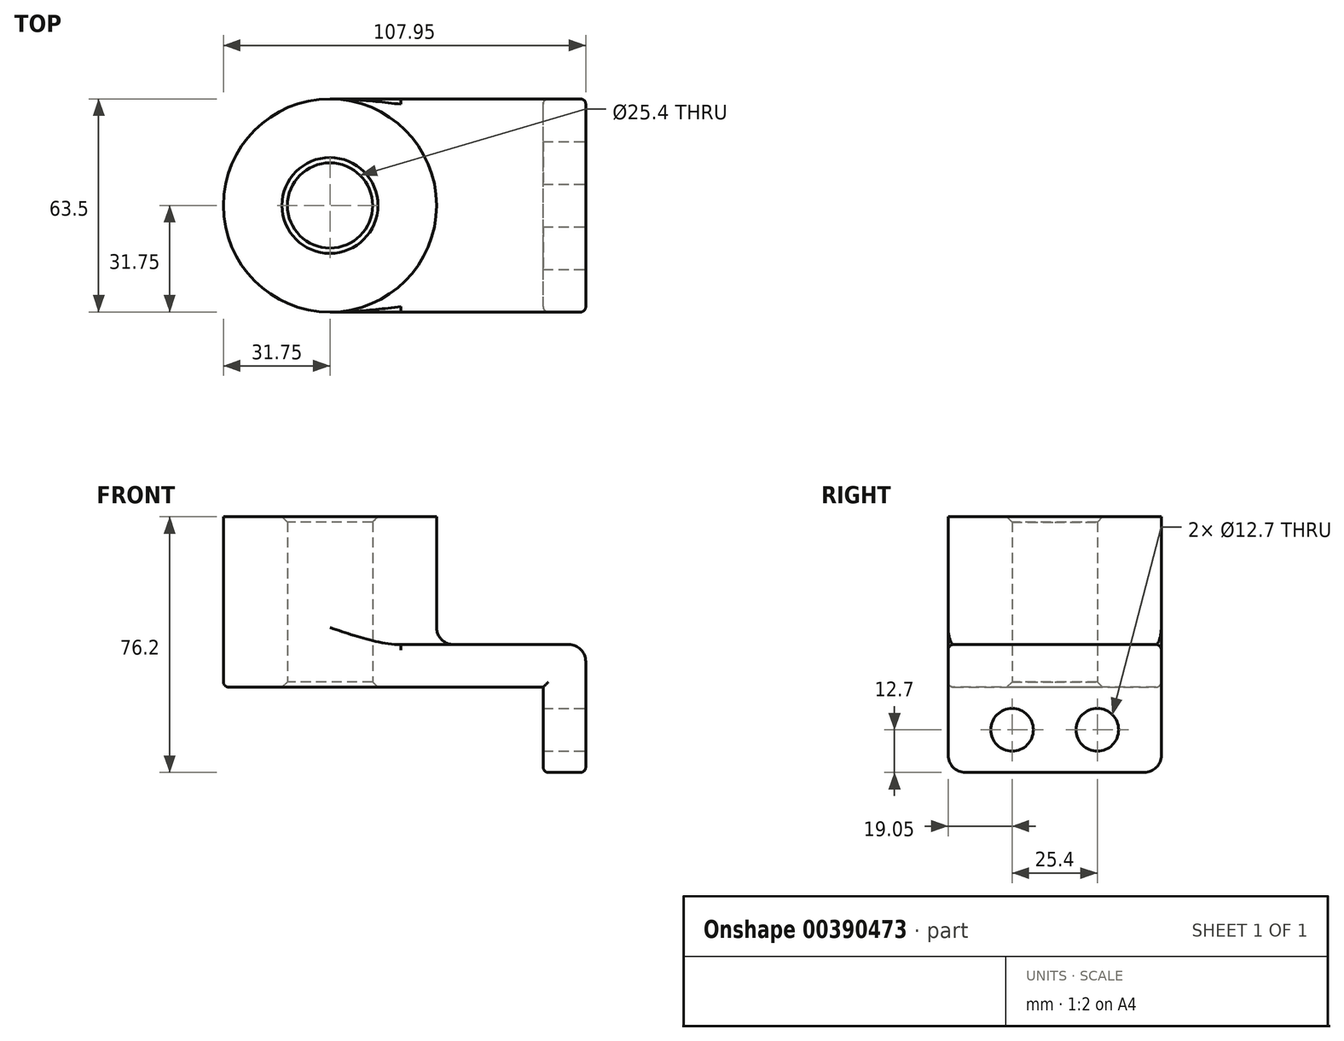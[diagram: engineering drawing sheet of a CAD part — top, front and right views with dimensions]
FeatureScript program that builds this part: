
annotation { "Feature Type Name" : "Feature", "Feature Type Description" : "" }
export const myFeature = defineFeature(function(context is Context, id is Id, definition is map)
    precondition{}
    {
        {
            var Q0;
            Q0=qCreatedBy(makeId("Top.planeOp"),FACE);
            var sketch = newSketch(context, id + "F0", { "sketchPlane" : qUnion([Q0])});
            skLineSegment(sketch, "E0.bottom", {"start": v(38.1, -31.75) * mm, "end": v(-38.1, -31.75) * mm});
            skLineSegment(sketch, "E0.top", {"start": v(38.1, 31.75) * mm, "end": v(-38.1, 31.75) * mm});
            skLineSegment(sketch, "E0.left", {"start": v(38.1, -31.75) * mm, "end": v(38.1, 31.75) * mm});
            skLineSegment(sketch, "E0.right", {"start": v(-38.1, -31.75) * mm, "end": v(-38.1, 31.75) * mm});
            skPoint(sketch, "E0.middle", {"position": v(0, 0) * mm});
            skCircle(sketch, "E1", {"center": v(-38.1, 0) * mm, "radius": 31.75 * mm});
            skCircle(sketch, "E2", {"center": v(-38.1, 0) * mm, "radius": 12.7 * mm});
            skSolve(sketch);
        }
        {
            var Q0;
            Q0 = qSketchRegion(id + "F0", true);
            extrude(context, id + "F1", {"entities" : qUnion([Q0]), "depth" : 12.7 * mm});
        }
        {
            var Q0;
            {var subQ1=sQuery(id+"F0.wireOp",EDGE,"E0.right");var subQ3=sQuery(id+"F0.wireOp",EDGE,"E2");var subQ4=makeQuery(id+"F0.imprint","INTERSECT",VERTEX,{"disambiguationData":[OD(0.0)],"derivedFrom":[subQ1,subQ3]});Q0=makeQuery(id+"F0.imprint","IMPRINT",FACE,{"disambiguationData":[TD([[makeQuery(id+"F0.imprint","IMPRINT",EDGE,{"disambiguationData":[TD([[subQ4,1.0]])],"derivedFrom":subQ3}),-1.0]])]});}
            var Q1;
            {var subQ1=sQuery(id+"F0.wireOp",EDGE,"E0.right");var subQ3=sQuery(id+"F0.wireOp",EDGE,"E2");var subQ4=makeQuery(id+"F0.imprint","INTERSECT",VERTEX,{"disambiguationData":[OD(0.0)],"derivedFrom":[subQ1,subQ3]});Q1=makeQuery(id+"F0.imprint","IMPRINT",FACE,{"disambiguationData":[TD([[makeQuery(id+"F0.imprint","IMPRINT",EDGE,{"disambiguationData":[TD([[subQ4,-1.0]])],"derivedFrom":subQ3}),-1.0]])]});}
            extrude(context, id + "F2", {"entities" : qUnion([Q0, Q1]), "operationType" : NewBodyOperationType.ADD, "depth" : 50.8 * mm});
        }
        {
            var Q0;
            Q0=makeQuery(id+"F1.opExtrude","SWEPT_FACE",FACE,{"disambiguationData":[OSD([sQuery(id+"F0.wireOp",EDGE,"E0.left")])]});
            var sketch = newSketch(context, id + "F3", { "sketchPlane" : qUnion([Q0])});
            skLineSegment(sketch, "E3.bottom", {"start": v(-31.75, 12.7) * mm, "end": v(31.75, 12.7) * mm});
            skLineSegment(sketch, "E3.top", {"start": v(-31.75, -25.4) * mm, "end": v(31.75, -25.4) * mm});
            skLineSegment(sketch, "E3.left", {"start": v(-31.75, 12.7) * mm, "end": v(-31.75, -25.4) * mm});
            skLineSegment(sketch, "E3.right", {"start": v(31.75, 12.7) * mm, "end": v(31.75, -25.4) * mm});
            skCircle(sketch, "E4", {"center": v(-12.7, -12.7) * mm, "radius": 6.35 * mm});
            skLineSegment(sketch, "E5", {"start": v(0, 12.7) * mm, "end": v(0, -25.4) * mm, "construction": true});
            skCircle(sketch, "E6.MirrorC", {"center": v(12.7, -12.7) * mm, "radius": 6.35 * mm});
            skSolve(sketch);
        }
        {
            var Q0;
            {var subQ2=sQuery(id+"F3.wireOp",EDGE,"E3.top");Q0=makeQuery(id+"F3.imprint","IMPRINT",FACE,{"disambiguationData":[TD([[makeQuery(id+"F3.imprint","IMPRINT",EDGE,{"derivedFrom":subQ2}),1.0]])]});}
            var Q1;
            {var subQ0=sQuery(id+"F3.wireOp",EDGE,"E3.bottom");Q1=makeQuery(id+"F3.imprint","IMPRINT",FACE,{"disambiguationData":[TD([[makeQuery(id+"F3.imprint","IMPRINT",EDGE,{"derivedFrom":subQ0}),-1.0]])]});}
            extrude(context, id + "F4", {"entities" : qUnion([Q0, Q1]), "operationType" : NewBodyOperationType.ADD, "oppositeDirection" : true, "depth" : 12.7 * mm});
        }
        {
            var Q0;
            {var subQ0=sQuery(id+"F0.wireOp",EDGE,"E1");Q0=makeQuery(id+"F2.boolean.opBoolean","INTERSECT",EDGE,{"derivedFrom":[makeQuery(id+"F1.opExtrude","CAP_FACE",FACE,{"disambiguationData":[OSD([sQuery(id+"F0.wireOp",EDGE,"E0.bottom"),sQuery(id+"F0.wireOp",EDGE,"E0.top"),sQuery(id+"F0.wireOp",EDGE,"E0.left"),subQ0,sQuery(id+"F0.wireOp",EDGE,"E2")])],"isStart":false}),makeQuery(id+"F2.opExtrude","SWEPT_FACE",FACE,{"disambiguationData":[OSD([subQ0])]})]});}
            var Q1;
            Q1=makeQuery(id+"F1.opExtrude","CAP_EDGE",EDGE,{"disambiguationData":[OSD([sQuery(id+"F0.wireOp",EDGE,"E0.left")])],"isStart":false});
            var Q2;
            Q2=makeQuery(id+"F4.opExtrude","SWEPT_EDGE",EDGE,{"disambiguationData":[OSD([sQuery(id+"F3.wireOp",EDGE,"E3.top"),sQuery(id+"F3.wireOp",EDGE,"E3.left")])]});
            var Q3;
            Q3=makeQuery(id+"F4.opExtrude","SWEPT_EDGE",EDGE,{"disambiguationData":[OSD([sQuery(id+"F3.wireOp",EDGE,"E3.top"),sQuery(id+"F3.wireOp",EDGE,"E3.right")])]});
            fillet(context, id + "F5", {"entities" : qUnion([Q0, Q1, Q2, Q3]), "radius" : 5.08 * mm, "tangentPropagation" : true, "allowEdgeOverflow" : false});
        }
        {
            var Q0;
            Q0=makeQuery(id+"F1.opExtrude","CAP_EDGE",EDGE,{"disambiguationData":[OSD([sQuery(id+"F0.wireOp",EDGE,"E0.bottom")])],"isStart":false});
            var Q1;
            Q1=makeQuery(id+"F1.opExtrude","CAP_EDGE",EDGE,{"disambiguationData":[OSD([sQuery(id+"F0.wireOp",EDGE,"E0.bottom")])],"isStart":true});
            var Q2;
            Q2=makeQuery(id+"F4.opExtrude","CAP_EDGE",EDGE,{"disambiguationData":[OSD([sQuery(id+"F3.wireOp",EDGE,"E3.left")])],"isStart":false});
            fillet(context, id + "F6", {"entities" : qUnion([Q0, Q1, Q2]), "radius" : 1.59 * mm, "tangentPropagation" : true, "allowEdgeOverflow" : false});
        }
        {
            var Q0;
            {var subQ0=sQuery(id+"F0.wireOp",EDGE,"E2");Q0=makeQuery(id+"F2.boolean.opBoolean","MERGE",FACE,{"derivedFrom":[makeQuery(id+"F1.opExtrude","SWEPT_FACE",FACE,{"disambiguationData":[OSD([subQ0])]}),makeQuery(id+"F2.opExtrude","SWEPT_FACE",FACE,{"disambiguationData":[OSD([subQ0])]})]});}
            chamfer(context, id + "F7", {"entities" : qUnion([Q0]), "width" : 1.59 * mm, "tangentPropagation" : true});
        }
    });
